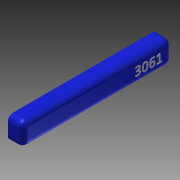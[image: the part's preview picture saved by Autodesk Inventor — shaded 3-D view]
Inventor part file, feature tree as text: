
AUTODESK INVENTOR PART (.ipt)
format: ipt  version: 2014 SP1 (Build 180222100, 222)  size: 364,544 bytes
history: native  units: in
note: dims shown in document units (in); Inventor stores cm internally (conversion verified against a paired STEP export)
features: reference x7, extrude x4, sketch x3, fillet x1, projected_geometry x1
ambient origin geometry x8: Origin, YZ Plane, XZ Plane, XY Plane, X Axis, Y Axis, Z Axis, Center Point
bodies: Solid1 (feature_tree)
feature tree (16):
  sketch  "Sketch1"  dims[d0=0.0625in d1=0.0in d3=1.0in]
  extrude  "Extrusion1"  Depth=1.0in
  extrude  "Extrusion2"  Depth=0.0625in
  extrude  "Extrusion3"  Depth=0.0625in TaperAngle=0.0deg
  fillet  "Fillet1"  Radius=1.3125in
  extrude  "Extrusion5"  Depth=0.0625in
  reference  "Reference4"
  reference  "Reference5"
  sketch  "Sketch2"  dims[d7=1.0in d9=0.0625in]
  reference  "Reference6"
  reference  "Reference7"
  reference  "Reference8"
  reference  "Reference9"
  reference  "Reference10"
  projected_geometry  "Projected Loop1"
  sketch  "Sketch4"  dims[d10=33.625in d11=0.0in d12=0.0625in d13=0.0in d14=1.3125in d20=0.0625in d21=0.0625in d26=1.0in d27=6.0in d28=2.5in d29=0.0625in d30=0.0in]
